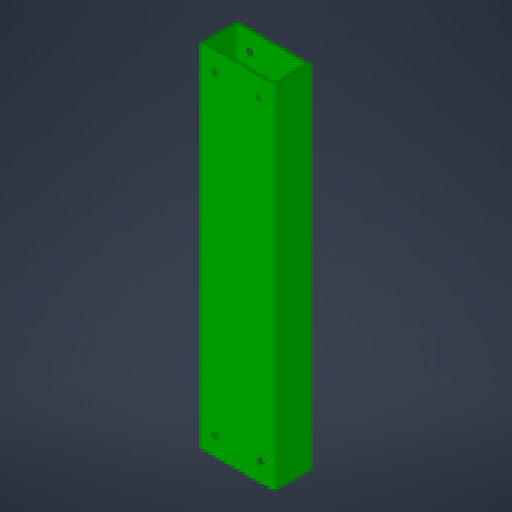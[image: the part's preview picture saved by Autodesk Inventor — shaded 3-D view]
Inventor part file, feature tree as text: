
AUTODESK INVENTOR PART (.ipt)
format: ipt  version: 2024 (Build 280153000, 153)  size: 164,864 bytes
history: native  units: mm
features: extrude x2, sketch x2
ambient origin geometry x8: Origin, YZ Plane, XZ Plane, XY Plane, X Axis, Y Axis, Z Axis, Center Point
bodies: Body1 (feature_tree)
feature tree (4):
  extrude  "Выдавливание3"  Depth=40.0mm
  extrude  "Выдавливание6"  Depth=190.0mm TaperAngle=0.0deg
  sketch  "Эскиз1"
  sketch  "Эскиз5"
